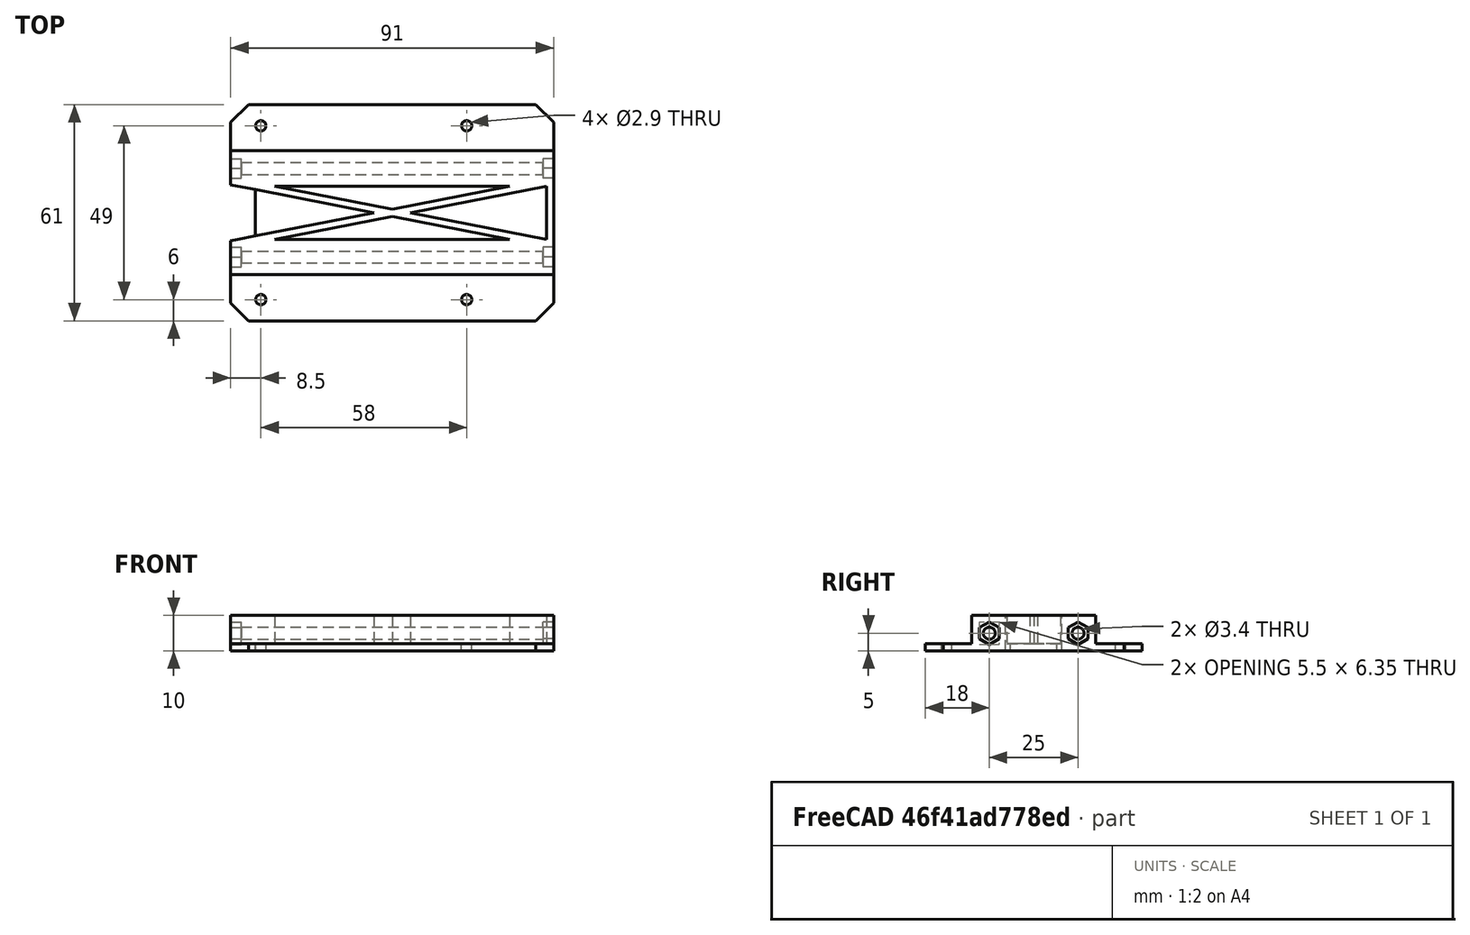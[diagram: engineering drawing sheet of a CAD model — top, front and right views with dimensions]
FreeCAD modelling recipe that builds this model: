
FCSTD DOCUMENT  (FreeCAD 0.21R33668 +26 (Git))
Label: Support_Raspi_new
License: All rights reserved
LicenseURL: https://en.wikipedia.org/wiki/All_rights_reserved
objects: Sketcher::SketchObject×7, PartDesign::Pocket×4, App::DocumentObjectGroup×3, PartDesign::CoordinateSystem×3, PartDesign::Hole×2, Spreadsheet::Sheet×1, PartDesign::Pad×1, App::FeaturePython×1, PartDesign::Chamfer×1, PartDesign::Body×1, App::Part×1, Mesh::Feature×1
note: 27 computed .brp shape members not serialized (recipe doc carries the construction recipe); baked Part::Feature solids carry a one-line shape summary decoded from their .brp
EXTERNAL_REF file=Raspberrypi4B.FCStd obj=Spreadsheet

FEATURE [Spreadsheet::Sheet] Spreadsheet
  cells = B2='walls_thickness; C2(walls_thickness)==2 mm; E2='width; F2(width)==main_case_width - walls_thickness * 2; H2='nut_depth; I2(nut_depth)==3 mm; B3='screw_radius; C3(screw_radius)==1.5 mm; E3='height; F3(height)==raspi_height + 5 mm; H3='nut_edge; I3(nut_edge)==5.5 mm; E4='depth; F4(depth)==10 mm; H4='raspi_nut_edge; I4(raspi_nut_edge)==4.5 mm; B5='raspi_width; C5(raspi_width)==<<Raspberrypi4B>>#<<Spreadsheet>>.width; E5='beam_width; F5(beam_width)==10 mm; B6='raspi_height; C6(raspi_height)==<<Raspberrypi4B>>#<<Spreadsheet>>.height; E6='carrier_holes_space; F6(carrier_holes_space)==25 mm; H6='main_case_width; I6(main_case_width)==95 mm; B7='raspi_holesH; C7(raspi_holesH)==<<Raspberrypi4B>>#<<Spreadsheet>>.holes_distH; E7='cross_thickness; F7(cross_thickness)==2 mm; B8='raspi_holesV; C8(raspi_holesV)==<<Raspberrypi4B>>#<<Spreadsheet>>.holes_distV; E8='pocket_sd_length; F8(pocket_sd_length)==5 mm; B9='raspi_holes_off_x; C9(raspi_holes_off_x)==<<Raspberrypi4B>>#<<Spreadsheet>>.holes_offset_x; E10='offset_to_right; F10(offset_to_right)==2 mm; E11='screw_left_dist; F11(screw_left_dist)==raspi_width / 2 - raspi_holes_off_x - offset_to_right
FEATURE [Sketcher::SketchObject] Sketch
  FullyConstrained = true
  MapMode = 5
  Support = -> [XY_Plane]
  expr: Constraints[10] = Spreadsheet.height
  expr: Constraints[9] = Spreadsheet.width
  sketch-geometry (4):
    g0: LineSegment StartX=-45.5 StartY=30.5 StartZ=0 EndX=45.5 EndY=30.5 EndZ=0
    g1: LineSegment StartX=45.5 StartY=30.5 StartZ=0 EndX=45.5 EndY=-30.5 EndZ=0
    g2: LineSegment StartX=45.5 StartY=-30.5 StartZ=0 EndX=-45.5 EndY=-30.5 EndZ=0
    g3: LineSegment StartX=-45.5 StartY=-30.5 StartZ=0 EndX=-45.5 EndY=30.5 EndZ=0
  constraints (11):
    c: Coincident(g0,g1)
    c: Coincident(g1,g2)
    c: Coincident(g2,g3)
    c: Coincident(g3,g0)
    c: Horizontal(g0)
    c: Horizontal(g2)
    c: Vertical(g1)
    c: Vertical(g3)
    c: Symmetric(g0,g1,g-1)
    c: DistanceX(g0,g0) = 91
    c: DistanceY(g3,g3) = 61
FEATURE [PartDesign::Pad] Pad
  Direction = (0,0,1)
  Length = 10
  Length2 = 10
  Profile = -> Sketch
  ReferenceAxis = -> Sketch [N_Axis]
  Type = 0
  expr: Length = Spreadsheet.depth
FEATURE [Sketcher::SketchObject] Sketch001
  ExternalGeometry = -> [Pad]
  FullyConstrained = true
  MapMode = 5
  Placement = pos=(0,0,10) rot=(0,0,1;0rad)
  Support = -> [Pad]
  expr: Constraints[47] = Spreadsheet.walls_thickness
  expr: Constraints[48] = Spreadsheet.beam_width
  expr: Constraints[50] = Spreadsheet.carrier_holes_space - Spreadsheet.beam_width
  expr: Constraints[70] = Spreadsheet.cross_thickness
  sketch-geometry (29):
    g0: LineSegment StartX=-45.5 StartY=30.5 StartZ=0 EndX=45.5 EndY=30.5 EndZ=0
    g1: LineSegment StartX=45.5 StartY=30.5 StartZ=0 EndX=45.5 EndY=17.5 EndZ=0
    g2: LineSegment StartX=45.5 StartY=17.5 StartZ=0 EndX=-45.5 EndY=17.5 EndZ=0
    g3: LineSegment StartX=-45.5 StartY=17.5 StartZ=0 EndX=-45.5 EndY=30.5 EndZ=0
    g4: LineSegment StartX=-45.5 StartY=-30.5 StartZ=0 EndX=45.5 EndY=-30.5 EndZ=0
    g5: LineSegment StartX=45.5 StartY=-30.5 StartZ=0 EndX=45.5 EndY=-17.5 EndZ=0
    g6: LineSegment StartX=45.5 StartY=-17.5 StartZ=0 EndX=-45.5 EndY=-17.5 EndZ=0
    g7: LineSegment StartX=-45.5 StartY=-17.5 StartZ=0 EndX=-45.5 EndY=-30.5 EndZ=0
    g8: LineSegment StartX=-33.0935 StartY=7.5 StartZ=0 EndX=0 EndY=1.019 EndZ=0
    g9: LineSegment StartX=0 StartY=1.019 StartZ=0 EndX=33.0935 EndY=7.5 EndZ=0
    g10: LineSegment StartX=33.0935 StartY=7.5 StartZ=0 EndX=-33.0935 EndY=7.5 EndZ=0
    g11: LineSegment StartX=-43.5 StartY=7.5 StartZ=0 EndX=-5.20323 EndY=0 EndZ=0
    g12: LineSegment StartX=-5.20323 StartY=0 StartZ=0 EndX=-43.5 EndY=-7.5 EndZ=0
    g13: LineSegment StartX=-43.5 StartY=-7.5 StartZ=0 EndX=-43.5 EndY=7.5 EndZ=0
    g14: LineSegment StartX=-33.0935 StartY=-7.5 StartZ=0 EndX=0 EndY=-1.019 EndZ=0
    g15: LineSegment StartX=0 StartY=-1.019 StartZ=0 EndX=33.0935 EndY=-7.5 EndZ=0
    g16: LineSegment StartX=33.0935 StartY=-7.5 StartZ=0 EndX=-33.0935 EndY=-7.5 EndZ=0
    g17: LineSegment StartX=43.5 StartY=-7.5 StartZ=0 EndX=5.20323 EndY=0 EndZ=0
    g18: LineSegment StartX=5.20323 StartY=0 StartZ=0 EndX=43.5 EndY=7.5 EndZ=0
    g19: LineSegment StartX=43.5 StartY=7.5 StartZ=0 EndX=43.5 EndY=-7.5 EndZ=0
    g20: LineSegment StartX=-43.5 StartY=7.5 StartZ=0 EndX=43.5 EndY=7.5 EndZ=0
    g21: LineSegment StartX=43.5 StartY=7.5 StartZ=0 EndX=43.5 EndY=-7.5 EndZ=0
    g22: LineSegment StartX=43.5 StartY=-7.5 StartZ=0 EndX=-43.5 EndY=-7.5 EndZ=0
    g23: LineSegment StartX=-43.5 StartY=-7.5 StartZ=0 EndX=-43.5 EndY=7.5 EndZ=0
    g24: LineSegment StartX=0 StartY=1.019 StartZ=0 EndX=5.20323 EndY=0 EndZ=0
    g25: LineSegment StartX=5.20323 StartY=0 StartZ=0 EndX=0 EndY=-1.019 EndZ=0
    g26: LineSegment StartX=0 StartY=-1.019 StartZ=0 EndX=-5.20323 EndY=0 EndZ=0
    g27: LineSegment StartX=-5.20323 StartY=0 StartZ=0 EndX=0 EndY=1.019 EndZ=0
    g28: LineSegment StartX=-33.0935 StartY=7.5 StartZ=0 EndX=-33.4779 EndY=5.53728 EndZ=0
  constraints (72):
    c: Coincident(g0,g1)
    c: Coincident(g1,g2)
    c: Coincident(g2,g3)
    c: Coincident(g3,g0)
    c: Coincident(g0,g-4)
    c: PointOnObject(g1,g-6)
    c: Coincident(g4,g5)
    c: Coincident(g5,g6)
    c: Coincident(g6,g7)
    c: Coincident(g7,g4)
    c: Coincident(g4,g-5)
    c: Symmetric(g2,g6,g-1)
    c: PointOnObject(g2,g-4)
    c: Symmetric(g1,g5,g-1)
    c: PointOnObject(g8,g-2)
    c: Coincident(g8,g9)
    c: Coincident(g9,g10)
    c: Coincident(g10,g8)
    c: PointOnObject(g11,g-1)
    c: Coincident(g11,g12)
    c: Coincident(g12,g13)
    c: Coincident(g13,g11)
    c: PointOnObject(g14,g-2)
    c: Coincident(g14,g15)
    c: Coincident(g15,g16)
    c: Coincident(g16,g14)
    c: PointOnObject(g17,g-1)
    c: Coincident(g17,g18)
    c: Coincident(g18,g19)
    c: Coincident(g19,g17)
    c: Coincident(g20,g21)
    c: Coincident(g21,g22)
    c: Coincident(g22,g23)
    c: Coincident(g23,g20)
    c: Vertical(g21)
    c: Coincident(g11,g20)
    c: Coincident(g21,g17)
    c: Coincident(g18,g20)
    c: Coincident(g12,g22)
    c: Vertical(g13)
    c: Horizontal(g20)
    c: Horizontal(g22)
    c: PointOnObject(g8,g20)
    c: PointOnObject(g9,g20)
    c: PointOnObject(g14,g22)
    c: PointOnObject(g15,g22)
    c: Symmetric(g11,g17,g-1)
    c: DistanceX(g2,g11) = 2
    c: DistanceY(g11,g2) = 10
    c: Horizontal(g2)
    c: DistanceY(g13,g13) = 15
    c: Coincident(g4,g-6)
    c: Coincident(g0,g-6)
    c: Coincident(g8,g24)
    c: Coincident(g24,g17)
    c: Coincident(g24,g25)
    c: Coincident(g25,g14)
    c: Coincident(g25,g26)
    c: Coincident(g26,g11)
    c: Coincident(g26,g27)
    c: Coincident(g27,g24)
    c: Parallel(g24,g8)
    c: Parallel(g24,g17)
    c: Parallel(g25,g18)
    c: Parallel(g25,g14)
    c: Parallel(g26,g11)
    c: Parallel(g26,g15)
    c: Coincident(g28,g8)
    c: PointOnObject(g28,g11)
    c: Perpendicular(g11,g28)
    c: Distance(g28) = 2
    c: Parallel(g27,g9)
FEATURE [PartDesign::Pocket] Pocket
  BaseFeature = -> Pad
  Direction = (0,0,-1)
  Length = 8
  Length2 = 5
  Profile = -> Sketch001
  ReferenceAxis = -> Sketch001 [N_Axis]
  Type = 0
  expr: Length = Spreadsheet.depth - Spreadsheet.walls_thickness
FEATURE [Sketcher::SketchObject] Sketch002
  ExternalGeometry = -> [Pocket]
  FullyConstrained = true
  MapMode = 5
  Placement = pos=(0,0,0) rot=(1,0,0;3.14159rad)
  Support = -> [Pocket]
  expr: Constraints[11] = <<Spreadsheet>>.raspi_holesH
  expr: Constraints[12] = <<Spreadsheet>>.raspi_holesV
  expr: Constraints[14] = <<Spreadsheet>>.screw_left_dist
  expr: Constraints[15] = Spreadsheet.screw_radius
  expr: Constraints[16] = Spreadsheet.screw_radius
  expr: Constraints[17] = Spreadsheet.screw_radius
  expr: Constraints[18] = Spreadsheet.screw_radius
  sketch-geometry (8):
    g0: LineSegment StartX=-37 StartY=24.5 StartZ=0 EndX=21 EndY=24.5 EndZ=0
    g1: LineSegment StartX=21 StartY=24.5 StartZ=0 EndX=21 EndY=-24.5 EndZ=0
    g2: LineSegment StartX=21 StartY=-24.5 StartZ=0 EndX=-37 EndY=-24.5 EndZ=0
    g3: LineSegment StartX=-37 StartY=-24.5 StartZ=0 EndX=-37 EndY=24.5 EndZ=0
    g4: Circle CenterX=-37 CenterY=24.5 CenterZ=0 NormalX=0 NormalY=0 NormalZ=1 AngleXU=0 Radius=1.5
    g5: Circle CenterX=21 CenterY=24.5 CenterZ=0 NormalX=0 NormalY=0 NormalZ=1 AngleXU=0 Radius=1.5
    g6: Circle CenterX=21 CenterY=-24.5 CenterZ=0 NormalX=0 NormalY=0 NormalZ=1 AngleXU=0 Radius=1.5
    g7: Circle CenterX=-37 CenterY=-24.5 CenterZ=0 NormalX=0 NormalY=0 NormalZ=1 AngleXU=0 Radius=1.5
  constraints (19):
    c: Coincident(g0,g1)
    c: Coincident(g1,g2)
    c: Coincident(g2,g3)
    c: Coincident(g3,g0)
    c: Horizontal(g0)
    c: Horizontal(g2)
    c: Vertical(g1)
    c: Coincident(g4,g0)
    c: Coincident(g5,g0)
    c: Coincident(g6,g1)
    c: Coincident(g7,g2)
    c: DistanceX(g0,g0) = 58
    c: DistanceY(g3,g3) = 49
    c: Symmetric(g4,g7,g-1)
    c: DistanceX(g4,g-1) = 37
    c: Radius(g4) = 1.5
    c: Radius(g5) = 1.5
    c: Radius(g7) = 1.5
    c: Radius(g6) = 1.5
FEATURE [PartDesign::Hole] Hole
  BaseFeature = -> Pocket
  CustomThreadClearance = 0
  Depth = 222.218
  DepthType = 1
  Diameter = 2.9
  DrillForDepth = false
  DrillPoint = 1
  DrillPointAngle = 118
  HoleCutCountersinkAngle = 90
  HoleCutCustomValues = false
  HoleCutDepth = 0
  HoleCutDiameter = 6.1
  HoleCutType = 0
  ModelThread = false
  Profile = -> Sketch002
  Tapered = false
  TaperedAngle = 90
  ThreadClass = 0
  ThreadDepth = 222.218
  ThreadDepthType = 0
  ThreadDirection = 0
  ThreadFit = 0
  ThreadSize = 8
  ThreadType = 1
  Threaded = false
  UseCustomThreadClearance = false
FEATURE [Sketcher::SketchObject] Sketch003
  ExternalGeometry = -> [Hole]
  FullyConstrained = true
  MapMode = 5
  Placement = pos=(-45.5,0,0) rot=(0.57735,-0.57735,-0.57735;2.0944rad)
  Support = -> [Hole]
  expr: Constraints[10] = Spreadsheet.screw_radius
  expr: Constraints[11] = Spreadsheet.screw_radius
  expr: Constraints[6] = Spreadsheet.beam_width
  expr: Constraints[7] = Spreadsheet.beam_width
  sketch-geometry (4):
    g0: LineSegment StartX=-7.5 StartY=10 StartZ=0 EndX=-7.5 EndY=0 EndZ=0
    g1: LineSegment StartX=7.5 StartY=10 StartZ=0 EndX=7.5 EndY=0 EndZ=0
    g2: Circle CenterX=-12.5 CenterY=5 CenterZ=0 NormalX=0 NormalY=0 NormalZ=1 AngleXU=0 Radius=1.5
    g3: Circle CenterX=12.5 CenterY=5 CenterZ=0 NormalX=0 NormalY=0 NormalZ=1 AngleXU=0 Radius=1.5
  constraints (12):
    c: PointOnObject(g0,g-4)
    c: PointOnObject(g0,g-6)
    c: Vertical(g0)
    c: PointOnObject(g1,g-4)
    c: PointOnObject(g1,g-6)
    c: Vertical(g1)
    c: DistanceX(g-4,g0) = 10
    c: DistanceX(g1,g-5) = 10
    c: Symmetric(g-4,g0,g2)
    c: Symmetric(g-5,g1,g3)
    c: Radius(g2) = 1.5
    c: Radius(g3) = 1.5
FEATURE [PartDesign::Hole] Hole001
  BaseFeature = -> Hole
  CustomThreadClearance = 0
  Depth = 222.218
  DepthType = 1
  Diameter = 3.4
  DrillForDepth = false
  DrillPoint = 1
  DrillPointAngle = 118
  HoleCutCountersinkAngle = 90
  HoleCutCustomValues = false
  HoleCutDepth = 0
  HoleCutDiameter = 6.1
  HoleCutType = 0
  ModelThread = false
  Profile = -> Sketch003
  Tapered = false
  TaperedAngle = 90
  ThreadClass = 0
  ThreadDepth = 222.218
  ThreadDepthType = 0
  ThreadDirection = 0
  ThreadFit = 0
  ThreadSize = 9
  ThreadType = 1
  Threaded = false
  UseCustomThreadClearance = false
FEATURE [Sketcher::SketchObject] Sketch004
  ExternalGeometry = -> [Hole001]
  FullyConstrained = true
  MapMode = 5
  Placement = pos=(-45.5,0,0) rot=(0.57735,-0.57735,-0.57735;2.0944rad)
  Support = -> [Hole001]
  expr: Constraints[38] = Spreadsheet.nut_edge
  expr: Constraints[39] = Spreadsheet.nut_edge
  sketch-geometry (14):
    g0: LineSegment StartX=-9.75 StartY=6.58771 StartZ=0 EndX=-12.5 EndY=8.17543 EndZ=0
    g1: LineSegment StartX=-12.5 StartY=8.17543 StartZ=0 EndX=-15.25 EndY=6.58771 EndZ=0
    g2: LineSegment StartX=-15.25 StartY=6.58771 StartZ=0 EndX=-15.25 EndY=3.41229 EndZ=0
    g3: LineSegment StartX=-15.25 StartY=3.41229 StartZ=0 EndX=-12.5 EndY=1.82457 EndZ=0
    g4: LineSegment StartX=-12.5 StartY=1.82457 StartZ=0 EndX=-9.75 EndY=3.41229 EndZ=0
    g5: LineSegment StartX=-9.75 StartY=3.41229 StartZ=0 EndX=-9.75 EndY=6.58771 EndZ=0
    g6: Circle CenterX=-12.5 CenterY=5 CenterZ=0 NormalX=0 NormalY=0 NormalZ=1 AngleXU=0 Radius=3.17543
    g7: LineSegment StartX=15.25 StartY=6.58771 StartZ=0 EndX=12.5 EndY=8.17543 EndZ=0
    g8: LineSegment StartX=12.5 StartY=8.17543 StartZ=0 EndX=9.75 EndY=6.58771 EndZ=0
    g9: LineSegment StartX=9.75 StartY=6.58771 StartZ=0 EndX=9.75 EndY=3.41229 EndZ=0
    g10: LineSegment StartX=9.75 StartY=3.41229 StartZ=0 EndX=12.5 EndY=1.82457 EndZ=0
    g11: LineSegment StartX=12.5 StartY=1.82457 StartZ=0 EndX=15.25 EndY=3.41229 EndZ=0
    g12: LineSegment StartX=15.25 StartY=3.41229 StartZ=0 EndX=15.25 EndY=6.58771 EndZ=0
    g13: Circle CenterX=12.5 CenterY=5 CenterZ=0 NormalX=0 NormalY=0 NormalZ=1 AngleXU=0 Radius=3.17543
  constraints (32):
    c: Coincident(g0,g1)
    c: Coincident(g1,g2)
    c: Coincident(g2,g3)
    c: Coincident(g3,g4)
    c: Coincident(g4,g5)
    c: Coincident(g5,g0)
    c: Equal(g0, g1-g5) x5
    c: PointOnObject(g0,g6)
    c: PointOnObject(g1,g6)
    c: PointOnObject(g2,g6)
    c: PointOnObject(g3,g6)
    c: PointOnObject(g4,g6)
    c: PointOnObject(g5,g6)
    c: Coincident(g6,g-3)
    c: Coincident(g7,g8)
    c: Coincident(g8,g9)
    c: Coincident(g9,g10)
    c: Coincident(g10,g11)
    c: Coincident(g11,g12)
    c: Coincident(g12,g7)
    c: Equal(g7, g8-g12) x5
    c: PointOnObject(g7,g13)
    c: PointOnObject(g8,g13)
    c: PointOnObject(g9,g13)
    c: PointOnObject(g10,g13)
    c: PointOnObject(g11,g13)
    c: PointOnObject(g12,g13)
    c: Coincident(g13,g-4)
    c: Vertical(g5)
    c: Vertical(g9)
    c: DistanceX(g1,g0) = 5.5
    c: DistanceX(g8,g7) = 5.5
FEATURE [PartDesign::Pocket] Pocket001
  BaseFeature = -> Hole001
  Direction = (1,0,0)
  Length = 3
  Length2 = 5
  Profile = -> Sketch004
  ReferenceAxis = -> Sketch004 [N_Axis]
  Type = 0
  expr: Length = Spreadsheet.nut_depth
FEATURE [Sketcher::SketchObject] Sketch005
  ExternalGeometry = -> [Pocket001]
  FullyConstrained = true
  MapMode = 5
  Placement = pos=(45.5,0,0) rot=(0.57735,0.57735,0.57735;2.0944rad)
  Support = -> [Pocket001]
  expr: Constraints[38] = Spreadsheet.nut_edge
  expr: Constraints[39] = Spreadsheet.nut_edge
  sketch-geometry (14):
    g0: LineSegment StartX=-9.75 StartY=6.58771 StartZ=0 EndX=-12.5 EndY=8.17543 EndZ=0
    g1: LineSegment StartX=-12.5 StartY=8.17543 StartZ=0 EndX=-15.25 EndY=6.58771 EndZ=0
    g2: LineSegment StartX=-15.25 StartY=6.58771 StartZ=0 EndX=-15.25 EndY=3.41229 EndZ=0
    g3: LineSegment StartX=-15.25 StartY=3.41229 StartZ=0 EndX=-12.5 EndY=1.82457 EndZ=0
    g4: LineSegment StartX=-12.5 StartY=1.82457 StartZ=0 EndX=-9.75 EndY=3.41229 EndZ=0
    g5: LineSegment StartX=-9.75 StartY=3.41229 StartZ=0 EndX=-9.75 EndY=6.58771 EndZ=0
    g6: Circle CenterX=-12.5 CenterY=5 CenterZ=0 NormalX=0 NormalY=0 NormalZ=1 AngleXU=0 Radius=3.17543
    g7: LineSegment StartX=15.25 StartY=6.58771 StartZ=0 EndX=12.5 EndY=8.17543 EndZ=0
    g8: LineSegment StartX=12.5 StartY=8.17543 StartZ=0 EndX=9.75 EndY=6.58771 EndZ=0
    g9: LineSegment StartX=9.75 StartY=6.58771 StartZ=0 EndX=9.75 EndY=3.41229 EndZ=0
    g10: LineSegment StartX=9.75 StartY=3.41229 StartZ=0 EndX=12.5 EndY=1.82457 EndZ=0
    g11: LineSegment StartX=12.5 StartY=1.82457 StartZ=0 EndX=15.25 EndY=3.41229 EndZ=0
    g12: LineSegment StartX=15.25 StartY=3.41229 StartZ=0 EndX=15.25 EndY=6.58771 EndZ=0
    g13: Circle CenterX=12.5 CenterY=5 CenterZ=0 NormalX=0 NormalY=0 NormalZ=1 AngleXU=0 Radius=3.17543
  constraints (32):
    c: Coincident(g0,g1)
    c: Coincident(g1,g2)
    c: Coincident(g2,g3)
    c: Coincident(g3,g4)
    c: Coincident(g4,g5)
    c: Coincident(g5,g0)
    c: Equal(g0, g1-g5) x5
    c: PointOnObject(g0,g6)
    c: PointOnObject(g1,g6)
    c: PointOnObject(g2,g6)
    c: PointOnObject(g3,g6)
    c: PointOnObject(g4,g6)
    c: PointOnObject(g5,g6)
    c: Coincident(g6,g-3)
    c: Coincident(g7,g8)
    c: Coincident(g8,g9)
    c: Coincident(g9,g10)
    c: Coincident(g10,g11)
    c: Coincident(g11,g12)
    c: Coincident(g12,g7)
    c: Equal(g7, g8-g12) x5
    c: PointOnObject(g7,g13)
    c: PointOnObject(g8,g13)
    c: PointOnObject(g9,g13)
    c: PointOnObject(g10,g13)
    c: PointOnObject(g11,g13)
    c: PointOnObject(g12,g13)
    c: Coincident(g13,g-4)
    c: Vertical(g5)
    c: Vertical(g9)
    c: DistanceX(g1,g0) = 5.5
    c: DistanceX(g8,g7) = 5.5
FEATURE [PartDesign::Pocket] Pocket002
  BaseFeature = -> Pocket001
  Direction = (-1,0,0)
  Length = 3
  Length2 = 5
  Profile = -> Sketch005
  ReferenceAxis = -> Sketch005 [N_Axis]
  Type = 0
  expr: Length = Spreadsheet.nut_depth
FEATURE [App::DocumentObjectGroup] Parts
FEATURE [PartDesign::CoordinateSystem] LCS_Origin
  AttacherType = Attacher::AttachEngine3D
  MapMode = 2
  Support = -> [X_Axis001]
FEATURE [App::DocumentObjectGroup] Constraints
FEATURE [App::FeaturePython] Variables  # WARN: FeaturePython — macro-defined, semantics opaque (R4)
  Type = App::PropertyContainer
FEATURE [App::DocumentObjectGroup] Configurations
FEATURE [PartDesign::CoordinateSystem] LCS_side
  AttacherType = Attacher::AttachEngine3D
  MapMode = 11
  Placement = pos=(45.5,-12.5,5) rot=(0.57735,-0.57735,0.57735;4.18879rad)
  Support = -> [Pocket001]
FEATURE [PartDesign::CoordinateSystem] LCS_raspi
  AttacherType = Attacher::AttachEngine3D
  MapMode = 11
  Placement = pos=(-37,-24.5,0) rot=(0.707107,0.707107,0;3.14159rad)
  Support = -> [Pocket001]
FEATURE [Sketcher::SketchObject] Sketch006
  ExternalGeometry = -> [Pocket001]
  FullyConstrained = true
  MapMode = 5
  Placement = pos=(0,0,0) rot=(1,0,0;3.14159rad)
  Support = -> [Pocket001]
  expr: Constraints[9] = Spreadsheet.pocket_sd_length + Spreadsheet.offset_to_right
  sketch-geometry (5):
    g0: LineSegment StartX=-45.5 StartY=7.89168 StartZ=0 EndX=-38.5 EndY=6.52081 EndZ=0
    g1: LineSegment StartX=-38.5 StartY=6.52081 StartZ=0 EndX=-38.5 EndY=-6.52081 EndZ=0
    g2: LineSegment StartX=-38.5 StartY=-6.52081 StartZ=0 EndX=-45.5 EndY=-7.89168 EndZ=0
    g3: LineSegment StartX=-45.5 StartY=-7.89168 StartZ=0 EndX=-45.5 EndY=7.89168 EndZ=0
    g4: GeomPoint X=-45.5 Y=0 Z=0
  constraints (13):
    c: Coincident(g0,g1)
    c: Coincident(g1,g2)
    c: Coincident(g2,g3)
    c: Coincident(g3,g0)
    c: Vertical(g1)
    c: Vertical(g3)
    c: PointOnObject(g4,g-3)
    c: PointOnObject(g4,g-1)
    c: Symmetric(g0,g2,g4)
    c: DistanceX(g0,g0) = 7
    c: PointOnObject(g1,g-5)
    c: PointOnObject(g0,g-4)
    c: PointOnObject(g-4,g0)
FEATURE [PartDesign::Pocket] Pocket003
  BaseFeature = -> Pocket002
  Direction = (0,0,1)
  Length = 5
  Length2 = 5
  Profile = -> Sketch006
  ReferenceAxis = -> Sketch006 [N_Axis]
  Type = 1
FEATURE [PartDesign::Chamfer] Chamfer
  Angle = 45
  Base = -> Pocket003 [Edge47,Edge4,Edge2,Edge16]
  BaseFeature = -> Pocket003
  ChamferType = 0
  FlipDirection = false
  Size = 5
  Size2 = 1
  SupportTransform = false
  UseAllEdges = false
FEATURE [PartDesign::Body] Body  label="Körper"
  Group = -> [Sketch,Pad,Sketch001,Pocket,Sketch002,Hole,Sketch003,Hole001,Sketch004,Pocket001,Sketch005,Pocket002,Sketch006,Pocket003,Chamfer]
  Origin = -> Origin
  Tip = -> Chamfer
FEATURE [App::Part] Model
  AssemblyType = Part::Link
  Group = -> [LCS_Origin,Constraints,Variables,Configurations,Body,LCS_side,LCS_raspi]
  Origin = -> Origin001
  Type = Assembly
FEATURE [Mesh::Feature] Mesh  label="Körper (Meshed)"
